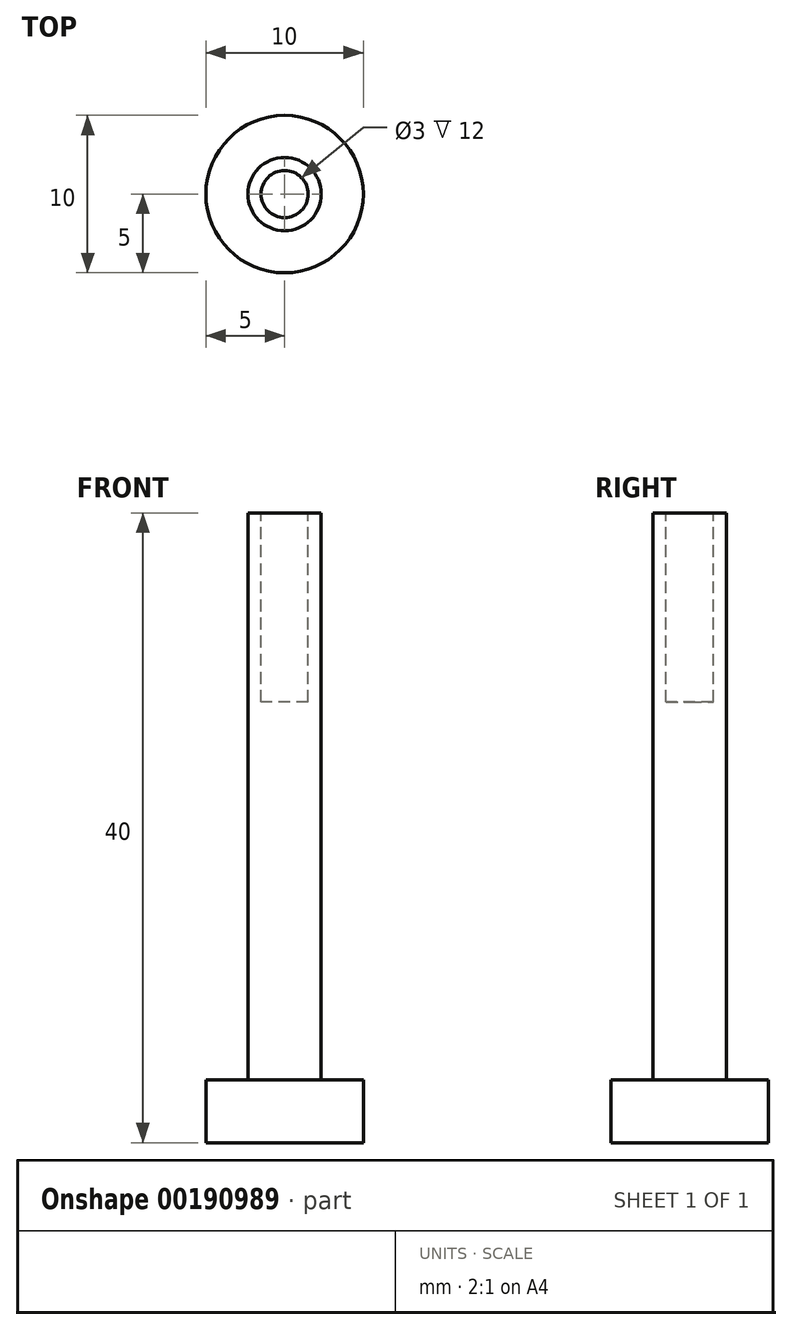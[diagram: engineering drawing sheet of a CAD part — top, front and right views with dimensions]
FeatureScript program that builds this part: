
annotation { "Feature Type Name" : "Feature", "Feature Type Description" : "" }
export const myFeature = defineFeature(function(context is Context, id is Id, definition is map)
    precondition{}
    {
        {
            var Q0;
            Q0=qCreatedBy(makeId("Top.planeOp"),FACE);
            var sketch = newSketch(context, id + "F0", { "sketchPlane" : qUnion([Q0])});
            skCircle(sketch, "E0", {"center": v(0, 0) * mm, "radius": 5 * mm});
            skCircle(sketch, "E1", {"center": v(0, 0) * mm, "radius": 2.33 * mm});
            skSolve(sketch);
        }
        {
            var Q0;
            Q0=makeQuery(id+"F0.imprint","IMPRINT",FACE,{"disambiguationData":[TD([[makeQuery(id+"F0.imprint","IMPRINT",EDGE,{"derivedFrom":sQuery(id+"F0.wireOp",EDGE,"E1")}),1.0]])]});
            extrude(context, id + "F1", {"entities" : qUnion([Q0]), "depth" : 40 * mm});
        }
        {
            var Q0;
            Q0=makeQuery(id+"F0.imprint","IMPRINT",FACE,{"disambiguationData":[TD([[makeQuery(id+"F0.imprint","IMPRINT",EDGE,{"derivedFrom":sQuery(id+"F0.wireOp",EDGE,"E0")}),1.0]])]});
            extrude(context, id + "F2", {"entities" : qUnion([Q0]), "operationType" : NewBodyOperationType.ADD, "depth" : 4 * mm});
        }
        {
            var Q0;
            Q0=makeQuery(id+"F1.opExtrude","CAP_FACE",FACE,{"disambiguationData":[OSD([sQuery(id+"F0.wireOp",EDGE,"E1")])],"isStart":false});
            var sketch = newSketch(context, id + "F3", { "sketchPlane" : qUnion([Q0])});
            skCircle(sketch, "E2", {"center": v(0, 0) * mm, "radius": 1.5 * mm});
            skSolve(sketch);
        }
        {
            var Q0;
            Q0=makeQuery(id+"F3.imprint","IMPRINT",FACE,{"disambiguationData":[TD([[makeQuery(id+"F3.imprint","IMPRINT",EDGE,{"derivedFrom":sQuery(id+"F3.wireOp",EDGE,"E2")}),1.0]])]});
            extrude(context, id + "F4", {"entities" : qUnion([Q0]), "operationType" : NewBodyOperationType.REMOVE, "oppositeDirection" : true, "depth" : 12 * mm});
        }
    });
